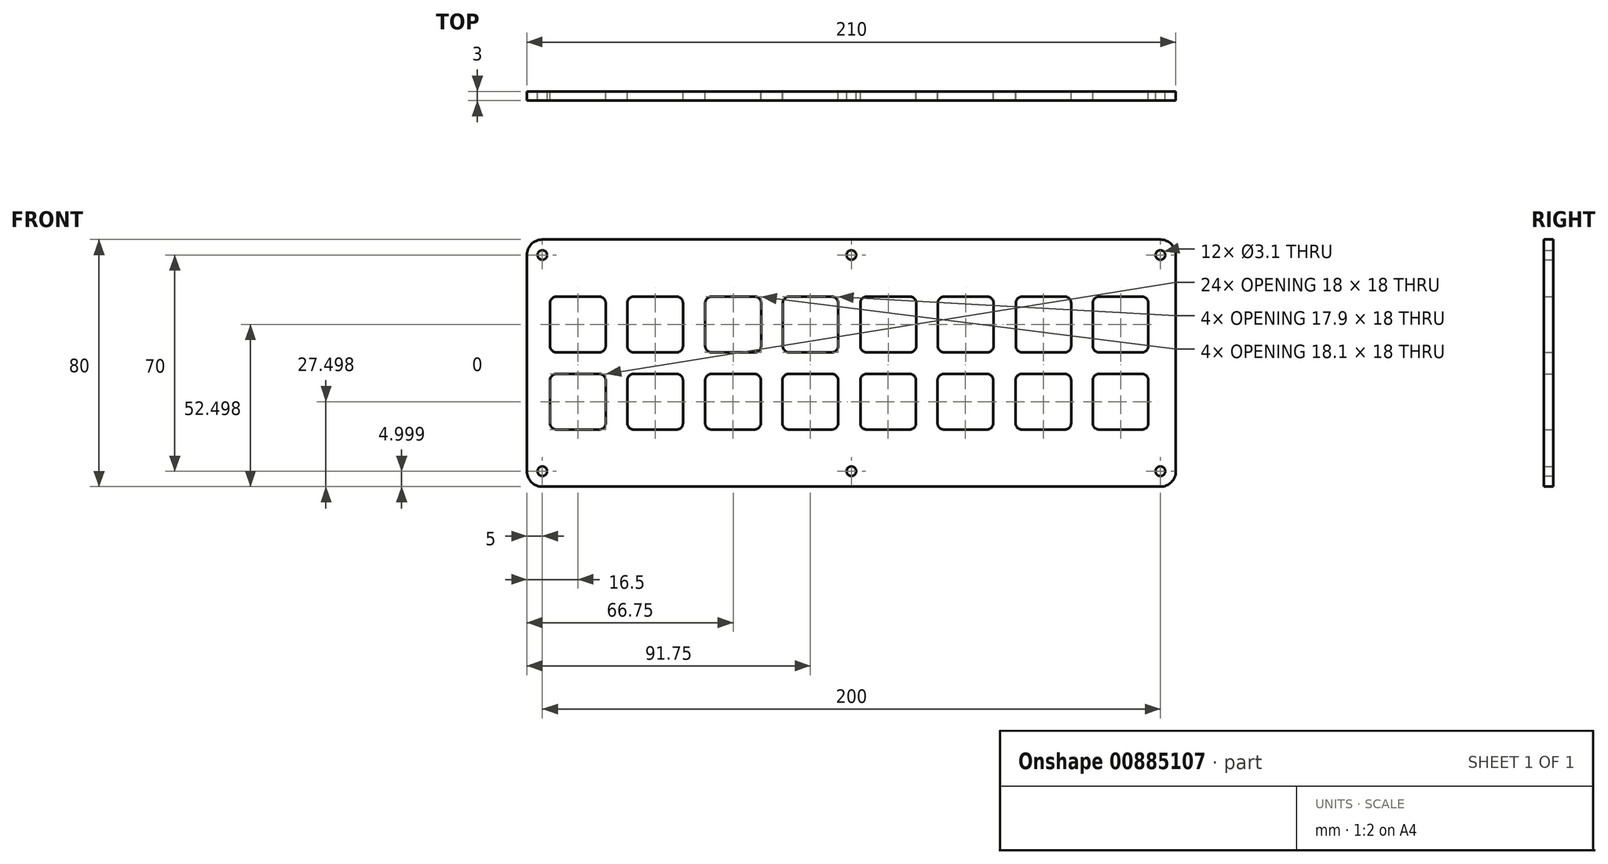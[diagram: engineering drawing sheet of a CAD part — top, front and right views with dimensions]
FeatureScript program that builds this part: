
annotation { "Feature Type Name" : "Feature", "Feature Type Description" : "" }
export const myFeature = defineFeature(function(context is Context, id is Id, definition is map)
    precondition{}
    {
        {
            var Q0;
            Q0=qCreatedBy(makeId("Front.planeOp"),FACE);
            var sketch = newSketch(context, id + "F0", { "sketchPlane" : qUnion([Q0])});
            skLineSegment(sketch, "E0.bottom", {"start": v(-115.46, 43.19) * mm, "end": v(84.54, 43.19) * mm});
            skLineSegment(sketch, "E0.top", {"start": v(-115.46, -36.81) * mm, "end": v(84.54, -36.81) * mm});
            skLineSegment(sketch, "E0.left", {"start": v(-120.46, 38.19) * mm, "end": v(-120.46, -31.81) * mm});
            skLineSegment(sketch, "E0.right", {"start": v(89.54, 38.19) * mm, "end": v(89.54, -31.81) * mm});
            skPoint(sketch, "E1.visualSharp", {"position": v(-120.46, 43.19) * mm});
            skArc(sketch, "E1.filletArc", {"start": v(-115.46, 43.19) * mm, "mid": v(-119, 41.72) * mm, "end": v(-120.46, 38.19) * mm});
            skPoint(sketch, "E2.visualSharp", {"position": v(-120.46, -36.81) * mm});
            skArc(sketch, "E2.filletArc", {"start": v(-120.46, -31.81) * mm, "mid": v(-119, -35.35) * mm, "end": v(-115.46, -36.81) * mm});
            skPoint(sketch, "E3.visualSharp", {"position": v(89.54, 43.19) * mm});
            skArc(sketch, "E3.filletArc", {"start": v(89.54, 38.19) * mm, "mid": v(88.08, 41.72) * mm, "end": v(84.54, 43.19) * mm});
            skPoint(sketch, "E4.visualSharp", {"position": v(89.54, -36.81) * mm});
            skArc(sketch, "E4.filletArc", {"start": v(84.54, -36.81) * mm, "mid": v(88.08, -35.35) * mm, "end": v(89.54, -31.81) * mm});
            skCircle(sketch, "E5", {"center": v(-115.46, 38.19) * mm, "radius": 1.55 * mm});
            skCircle(sketch, "E6", {"center": v(-115.46, -31.81) * mm, "radius": 1.55 * mm});
            skCircle(sketch, "E7", {"center": v(84.54, -31.81) * mm, "radius": 1.55 * mm});
            skCircle(sketch, "E8", {"center": v(84.54, 38.19) * mm, "radius": 1.55 * mm});
            skLineSegment(sketch, "E9.bottom", {"start": v(-110.96, 24.69) * mm, "end": v(-96.96, 24.69) * mm});
            skLineSegment(sketch, "E9.top", {"start": v(-110.96, 6.69) * mm, "end": v(-96.96, 6.69) * mm});
            skLineSegment(sketch, "E9.left", {"start": v(-112.96, 22.69) * mm, "end": v(-112.96, 8.69) * mm});
            skLineSegment(sketch, "E9.right", {"start": v(-94.96, 22.69) * mm, "end": v(-94.96, 8.69) * mm});
            skLineSegment(sketch, "E10.bottom", {"start": v(-71.96, 6.69) * mm, "end": v(-85.96, 6.69) * mm});
            skLineSegment(sketch, "E10.top", {"start": v(-71.96, 24.69) * mm, "end": v(-85.96, 24.69) * mm});
            skLineSegment(sketch, "E10.left", {"start": v(-69.96, 8.69) * mm, "end": v(-69.96, 22.69) * mm});
            skLineSegment(sketch, "E10.right", {"start": v(-87.96, 8.69) * mm, "end": v(-87.96, 22.69) * mm});
            skLineSegment(sketch, "E11.bottom", {"start": v(-110.96, -0.31) * mm, "end": v(-96.96, -0.31) * mm});
            skLineSegment(sketch, "E11.top", {"start": v(-110.96, -18.31) * mm, "end": v(-96.96, -18.31) * mm});
            skLineSegment(sketch, "E11.left", {"start": v(-112.96, -2.31) * mm, "end": v(-112.96, -16.31) * mm});
            skLineSegment(sketch, "E11.right", {"start": v(-94.96, -2.31) * mm, "end": v(-94.96, -16.31) * mm});
            skLineSegment(sketch, "E12.bottom", {"start": v(-85.96, -0.31) * mm, "end": v(-71.96, -0.31) * mm});
            skLineSegment(sketch, "E12.top", {"start": v(-85.96, -18.31) * mm, "end": v(-71.96, -18.31) * mm});
            skLineSegment(sketch, "E12.left", {"start": v(-87.96, -2.31) * mm, "end": v(-87.96, -16.31) * mm});
            skLineSegment(sketch, "E12.right", {"start": v(-69.96, -2.31) * mm, "end": v(-69.96, -16.31) * mm});
            skLineSegment(sketch, "E13.bottom", {"start": v(-60.76, 24.69) * mm, "end": v(-46.66, 24.69) * mm});
            skLineSegment(sketch, "E13.top", {"start": v(-60.76, 6.69) * mm, "end": v(-46.66, 6.69) * mm});
            skLineSegment(sketch, "E13.left", {"start": v(-62.76, 22.69) * mm, "end": v(-62.76, 8.69) * mm});
            skLineSegment(sketch, "E13.right", {"start": v(-44.66, 22.69) * mm, "end": v(-44.66, 8.69) * mm});
            skLineSegment(sketch, "E14.bottom", {"start": v(-35.66, 24.69) * mm, "end": v(-21.76, 24.69) * mm});
            skLineSegment(sketch, "E14.top", {"start": v(-35.66, 6.69) * mm, "end": v(-21.76, 6.69) * mm});
            skLineSegment(sketch, "E14.left", {"start": v(-37.66, 22.69) * mm, "end": v(-37.66, 8.69) * mm});
            skLineSegment(sketch, "E14.right", {"start": v(-19.76, 22.69) * mm, "end": v(-19.76, 8.69) * mm});
            skLineSegment(sketch, "E15.bottom", {"start": v(-60.76, -0.31) * mm, "end": v(-46.76, -0.31) * mm});
            skLineSegment(sketch, "E15.top", {"start": v(-60.76, -18.31) * mm, "end": v(-46.76, -18.31) * mm});
            skLineSegment(sketch, "E15.left", {"start": v(-62.76, -2.31) * mm, "end": v(-62.76, -16.31) * mm});
            skLineSegment(sketch, "E15.right", {"start": v(-44.76, -2.31) * mm, "end": v(-44.76, -16.31) * mm});
            skLineSegment(sketch, "E16.bottom", {"start": v(-35.76, -0.31) * mm, "end": v(-21.76, -0.31) * mm});
            skLineSegment(sketch, "E16.top", {"start": v(-35.76, -18.31) * mm, "end": v(-21.76, -18.31) * mm});
            skLineSegment(sketch, "E16.left", {"start": v(-37.76, -2.31) * mm, "end": v(-37.76, -16.31) * mm});
            skLineSegment(sketch, "E16.right", {"start": v(-19.76, -2.31) * mm, "end": v(-19.76, -16.31) * mm});
            skLineSegment(sketch, "E17.bottom", {"start": v(-10.56, 24.69) * mm, "end": v(3.54, 24.69) * mm});
            skLineSegment(sketch, "E17.top", {"start": v(-10.56, 6.69) * mm, "end": v(3.54, 6.69) * mm});
            skLineSegment(sketch, "E17.left", {"start": v(-12.56, 22.69) * mm, "end": v(-12.56, 8.69) * mm});
            skLineSegment(sketch, "E17.right", {"start": v(5.54, 22.69) * mm, "end": v(5.54, 8.69) * mm});
            skLineSegment(sketch, "E18.bottom", {"start": v(-10.56, -0.31) * mm, "end": v(3.44, -0.31) * mm});
            skLineSegment(sketch, "E18.top", {"start": v(-10.56, -18.31) * mm, "end": v(3.44, -18.31) * mm});
            skLineSegment(sketch, "E18.left", {"start": v(-12.56, -2.31) * mm, "end": v(-12.56, -16.31) * mm});
            skLineSegment(sketch, "E18.right", {"start": v(5.44, -2.31) * mm, "end": v(5.44, -16.31) * mm});
            skLineSegment(sketch, "E19.bottom", {"start": v(14.54, 24.69) * mm, "end": v(28.54, 24.69) * mm});
            skLineSegment(sketch, "E19.top", {"start": v(14.54, 6.69) * mm, "end": v(28.54, 6.69) * mm});
            skLineSegment(sketch, "E19.left", {"start": v(12.54, 22.69) * mm, "end": v(12.54, 8.69) * mm});
            skLineSegment(sketch, "E19.right", {"start": v(30.54, 22.69) * mm, "end": v(30.54, 8.69) * mm});
            skLineSegment(sketch, "E20.bottom", {"start": v(14.44, -0.31) * mm, "end": v(28.44, -0.31) * mm});
            skLineSegment(sketch, "E20.top", {"start": v(14.44, -18.31) * mm, "end": v(28.44, -18.31) * mm});
            skLineSegment(sketch, "E20.left", {"start": v(12.44, -2.31) * mm, "end": v(12.44, -16.31) * mm});
            skLineSegment(sketch, "E20.right", {"start": v(30.44, -2.31) * mm, "end": v(30.44, -16.31) * mm});
            skLineSegment(sketch, "E21.bottom", {"start": v(39.74, 24.69) * mm, "end": v(53.64, 24.69) * mm});
            skLineSegment(sketch, "E21.top", {"start": v(39.74, 6.69) * mm, "end": v(53.64, 6.69) * mm});
            skLineSegment(sketch, "E21.left", {"start": v(37.74, 22.69) * mm, "end": v(37.74, 8.69) * mm});
            skLineSegment(sketch, "E21.right", {"start": v(55.64, 22.69) * mm, "end": v(55.64, 8.69) * mm});
            skLineSegment(sketch, "E22.bottom", {"start": v(64.64, 24.69) * mm, "end": v(78.64, 24.69) * mm});
            skLineSegment(sketch, "E22.top", {"start": v(64.64, 6.69) * mm, "end": v(78.64, 6.69) * mm});
            skLineSegment(sketch, "E22.left", {"start": v(62.64, 22.69) * mm, "end": v(62.64, 8.69) * mm});
            skLineSegment(sketch, "E22.right", {"start": v(80.64, 22.69) * mm, "end": v(80.64, 8.69) * mm});
            skLineSegment(sketch, "E23.bottom", {"start": v(39.64, -0.31) * mm, "end": v(53.64, -0.31) * mm});
            skLineSegment(sketch, "E23.top", {"start": v(39.64, -18.31) * mm, "end": v(53.64, -18.31) * mm});
            skLineSegment(sketch, "E23.left", {"start": v(37.64, -2.31) * mm, "end": v(37.64, -16.31) * mm});
            skLineSegment(sketch, "E23.right", {"start": v(55.64, -2.31) * mm, "end": v(55.64, -16.31) * mm});
            skLineSegment(sketch, "E24.bottom", {"start": v(64.64, -0.31) * mm, "end": v(78.64, -0.31) * mm});
            skLineSegment(sketch, "E24.top", {"start": v(64.64, -18.31) * mm, "end": v(78.64, -18.31) * mm});
            skLineSegment(sketch, "E24.left", {"start": v(62.64, -2.31) * mm, "end": v(62.64, -16.31) * mm});
            skLineSegment(sketch, "E24.right", {"start": v(80.64, -2.31) * mm, "end": v(80.64, -16.31) * mm});
            skPoint(sketch, "E25", {"position": v(-15.46, 38.19) * mm});
            skCircle(sketch, "E26", {"center": v(-15.46, 38.19) * mm, "radius": 1.55 * mm});
            skPoint(sketch, "E27.visualSharp", {"position": v(-112.96, 24.69) * mm});
            skArc(sketch, "E27.filletArc", {"start": v(-110.96, 24.69) * mm, "mid": v(-112.37, 24.1) * mm, "end": v(-112.96, 22.69) * mm});
            skPoint(sketch, "E28.visualSharp", {"position": v(-94.96, 24.69) * mm});
            skArc(sketch, "E28.filletArc", {"start": v(-94.96, 22.69) * mm, "mid": v(-95.55, 24.1) * mm, "end": v(-96.96, 24.69) * mm});
            skPoint(sketch, "E29.visualSharp", {"position": v(-94.96, 6.69) * mm});
            skArc(sketch, "E29.filletArc", {"start": v(-96.96, 6.69) * mm, "mid": v(-95.55, 7.27) * mm, "end": v(-94.96, 8.69) * mm});
            skPoint(sketch, "E30.visualSharp", {"position": v(-112.96, 6.69) * mm});
            skArc(sketch, "E30.filletArc", {"start": v(-112.96, 8.69) * mm, "mid": v(-112.37, 7.27) * mm, "end": v(-110.96, 6.69) * mm});
            skPoint(sketch, "E31.visualSharp", {"position": v(-112.96, -0.31) * mm});
            skArc(sketch, "E31.filletArc", {"start": v(-110.96, -0.31) * mm, "mid": v(-112.37, -0.9) * mm, "end": v(-112.96, -2.31) * mm});
            skPoint(sketch, "E32.visualSharp", {"position": v(-94.96, -0.31) * mm});
            skArc(sketch, "E32.filletArc", {"start": v(-94.96, -2.31) * mm, "mid": v(-95.55, -0.9) * mm, "end": v(-96.96, -0.31) * mm});
            skPoint(sketch, "E33.visualSharp", {"position": v(-94.96, -18.31) * mm});
            skArc(sketch, "E33.filletArc", {"start": v(-96.96, -18.31) * mm, "mid": v(-95.55, -17.73) * mm, "end": v(-94.96, -16.31) * mm});
            skPoint(sketch, "E34.visualSharp", {"position": v(-112.96, -18.31) * mm});
            skArc(sketch, "E34.filletArc", {"start": v(-112.96, -16.31) * mm, "mid": v(-112.37, -17.73) * mm, "end": v(-110.96, -18.31) * mm});
            skPoint(sketch, "E35.visualSharp", {"position": v(-87.96, -0.31) * mm});
            skArc(sketch, "E35.filletArc", {"start": v(-85.96, -0.31) * mm, "mid": v(-87.37, -0.9) * mm, "end": v(-87.96, -2.31) * mm});
            skPoint(sketch, "E36.visualSharp", {"position": v(-69.96, -0.31) * mm});
            skArc(sketch, "E36.filletArc", {"start": v(-69.96, -2.31) * mm, "mid": v(-70.55, -0.9) * mm, "end": v(-71.96, -0.31) * mm});
            skPoint(sketch, "E37.visualSharp", {"position": v(-69.96, -18.31) * mm});
            skArc(sketch, "E37.filletArc", {"start": v(-71.96, -18.31) * mm, "mid": v(-70.55, -17.73) * mm, "end": v(-69.96, -16.31) * mm});
            skPoint(sketch, "E38.visualSharp", {"position": v(-87.96, -18.31) * mm});
            skArc(sketch, "E38.filletArc", {"start": v(-87.96, -16.31) * mm, "mid": v(-87.37, -17.73) * mm, "end": v(-85.96, -18.31) * mm});
            skPoint(sketch, "E39.visualSharp", {"position": v(-87.96, 24.69) * mm});
            skArc(sketch, "E39.filletArc", {"start": v(-85.96, 24.69) * mm, "mid": v(-87.37, 24.1) * mm, "end": v(-87.96, 22.69) * mm});
            skPoint(sketch, "E40.visualSharp", {"position": v(-69.96, 24.69) * mm});
            skArc(sketch, "E40.filletArc", {"start": v(-69.96, 22.69) * mm, "mid": v(-70.55, 24.1) * mm, "end": v(-71.96, 24.69) * mm});
            skPoint(sketch, "E41.visualSharp", {"position": v(-69.96, 6.69) * mm});
            skArc(sketch, "E41.filletArc", {"start": v(-71.96, 6.69) * mm, "mid": v(-70.55, 7.27) * mm, "end": v(-69.96, 8.69) * mm});
            skPoint(sketch, "E42.visualSharp", {"position": v(-87.96, 6.69) * mm});
            skArc(sketch, "E42.filletArc", {"start": v(-87.96, 8.69) * mm, "mid": v(-87.37, 7.27) * mm, "end": v(-85.96, 6.69) * mm});
            skPoint(sketch, "E43.visualSharp", {"position": v(-62.76, 24.69) * mm});
            skArc(sketch, "E43.filletArc", {"start": v(-60.76, 24.69) * mm, "mid": v(-62.17, 24.1) * mm, "end": v(-62.76, 22.69) * mm});
            skPoint(sketch, "E44.visualSharp", {"position": v(-44.66, 24.69) * mm});
            skArc(sketch, "E44.filletArc", {"start": v(-44.66, 22.69) * mm, "mid": v(-45.25, 24.1) * mm, "end": v(-46.66, 24.69) * mm});
            skPoint(sketch, "E45.visualSharp", {"position": v(-44.66, 6.69) * mm});
            skArc(sketch, "E45.filletArc", {"start": v(-46.66, 6.69) * mm, "mid": v(-45.25, 7.27) * mm, "end": v(-44.66, 8.69) * mm});
            skPoint(sketch, "E46.visualSharp", {"position": v(-62.76, 6.69) * mm});
            skArc(sketch, "E46.filletArc", {"start": v(-62.76, 8.69) * mm, "mid": v(-62.17, 7.27) * mm, "end": v(-60.76, 6.69) * mm});
            skPoint(sketch, "E47.visualSharp", {"position": v(-62.76, -0.31) * mm});
            skArc(sketch, "E47.filletArc", {"start": v(-60.76, -0.31) * mm, "mid": v(-62.17, -0.9) * mm, "end": v(-62.76, -2.31) * mm});
            skPoint(sketch, "E48.visualSharp", {"position": v(-44.76, -0.31) * mm});
            skArc(sketch, "E48.filletArc", {"start": v(-44.76, -2.31) * mm, "mid": v(-45.35, -0.9) * mm, "end": v(-46.76, -0.31) * mm});
            skPoint(sketch, "E49.visualSharp", {"position": v(-44.76, -18.31) * mm});
            skArc(sketch, "E49.filletArc", {"start": v(-46.76, -18.31) * mm, "mid": v(-45.35, -17.73) * mm, "end": v(-44.76, -16.31) * mm});
            skPoint(sketch, "E50.visualSharp", {"position": v(-62.76, -18.31) * mm});
            skArc(sketch, "E50.filletArc", {"start": v(-62.76, -16.31) * mm, "mid": v(-62.17, -17.73) * mm, "end": v(-60.76, -18.31) * mm});
            skPoint(sketch, "E51.visualSharp", {"position": v(-37.76, -18.31) * mm});
            skArc(sketch, "E51.filletArc", {"start": v(-37.76, -16.31) * mm, "mid": v(-37.17, -17.73) * mm, "end": v(-35.76, -18.31) * mm});
            skPoint(sketch, "E52.visualSharp", {"position": v(-37.76, -0.31) * mm});
            skArc(sketch, "E52.filletArc", {"start": v(-35.76, -0.31) * mm, "mid": v(-37.17, -0.9) * mm, "end": v(-37.76, -2.31) * mm});
            skPoint(sketch, "E53.visualSharp", {"position": v(-19.76, -0.31) * mm});
            skArc(sketch, "E53.filletArc", {"start": v(-19.76, -2.31) * mm, "mid": v(-20.35, -0.9) * mm, "end": v(-21.76, -0.31) * mm});
            skPoint(sketch, "E54.visualSharp", {"position": v(-19.76, -18.31) * mm});
            skArc(sketch, "E54.filletArc", {"start": v(-21.76, -18.31) * mm, "mid": v(-20.35, -17.73) * mm, "end": v(-19.76, -16.31) * mm});
            skPoint(sketch, "E55.visualSharp", {"position": v(-37.66, 6.69) * mm});
            skArc(sketch, "E55.filletArc", {"start": v(-37.66, 8.69) * mm, "mid": v(-37.07, 7.27) * mm, "end": v(-35.66, 6.69) * mm});
            skPoint(sketch, "E56.visualSharp", {"position": v(-37.66, 24.69) * mm});
            skArc(sketch, "E56.filletArc", {"start": v(-35.66, 24.69) * mm, "mid": v(-37.07, 24.1) * mm, "end": v(-37.66, 22.69) * mm});
            skPoint(sketch, "E57.visualSharp", {"position": v(-19.76, 24.69) * mm});
            skArc(sketch, "E57.filletArc", {"start": v(-19.76, 22.69) * mm, "mid": v(-20.35, 24.1) * mm, "end": v(-21.76, 24.69) * mm});
            skPoint(sketch, "E58.visualSharp", {"position": v(-19.76, 6.69) * mm});
            skArc(sketch, "E58.filletArc", {"start": v(-21.76, 6.69) * mm, "mid": v(-20.35, 7.27) * mm, "end": v(-19.76, 8.69) * mm});
            skPoint(sketch, "E59.visualSharp", {"position": v(-12.56, 24.69) * mm});
            skArc(sketch, "E59.filletArc", {"start": v(-10.56, 24.69) * mm, "mid": v(-11.97, 24.1) * mm, "end": v(-12.56, 22.69) * mm});
            skPoint(sketch, "E60.visualSharp", {"position": v(5.54, 24.69) * mm});
            skArc(sketch, "E60.filletArc", {"start": v(5.54, 22.69) * mm, "mid": v(4.95, 24.1) * mm, "end": v(3.54, 24.69) * mm});
            skPoint(sketch, "E61.visualSharp", {"position": v(5.54, 6.69) * mm});
            skArc(sketch, "E61.filletArc", {"start": v(3.54, 6.69) * mm, "mid": v(4.95, 7.27) * mm, "end": v(5.54, 8.69) * mm});
            skPoint(sketch, "E62.visualSharp", {"position": v(-12.56, 6.69) * mm});
            skArc(sketch, "E62.filletArc", {"start": v(-12.56, 8.69) * mm, "mid": v(-11.97, 7.27) * mm, "end": v(-10.56, 6.69) * mm});
            skPoint(sketch, "E63.visualSharp", {"position": v(-12.56, -0.31) * mm});
            skArc(sketch, "E63.filletArc", {"start": v(-10.56, -0.31) * mm, "mid": v(-11.97, -0.9) * mm, "end": v(-12.56, -2.31) * mm});
            skPoint(sketch, "E64.visualSharp", {"position": v(5.44, -0.31) * mm});
            skArc(sketch, "E64.filletArc", {"start": v(5.44, -2.31) * mm, "mid": v(4.85, -0.9) * mm, "end": v(3.44, -0.31) * mm});
            skPoint(sketch, "E65.visualSharp", {"position": v(5.44, -18.31) * mm});
            skArc(sketch, "E65.filletArc", {"start": v(3.44, -18.31) * mm, "mid": v(4.85, -17.73) * mm, "end": v(5.44, -16.31) * mm});
            skPoint(sketch, "E66.visualSharp", {"position": v(-12.56, -18.31) * mm});
            skArc(sketch, "E66.filletArc", {"start": v(-12.56, -16.31) * mm, "mid": v(-11.97, -17.73) * mm, "end": v(-10.56, -18.31) * mm});
            skPoint(sketch, "E67.visualSharp", {"position": v(12.44, -0.31) * mm});
            skArc(sketch, "E67.filletArc", {"start": v(14.44, -0.31) * mm, "mid": v(13.03, -0.9) * mm, "end": v(12.44, -2.31) * mm});
            skPoint(sketch, "E68.visualSharp", {"position": v(30.44, -0.31) * mm});
            skArc(sketch, "E68.filletArc", {"start": v(30.44, -2.31) * mm, "mid": v(29.85, -0.9) * mm, "end": v(28.44, -0.31) * mm});
            skPoint(sketch, "E69.visualSharp", {"position": v(30.44, -18.31) * mm});
            skArc(sketch, "E69.filletArc", {"start": v(28.44, -18.31) * mm, "mid": v(29.85, -17.73) * mm, "end": v(30.44, -16.31) * mm});
            skPoint(sketch, "E70.visualSharp", {"position": v(12.44, -18.31) * mm});
            skArc(sketch, "E70.filletArc", {"start": v(12.44, -16.31) * mm, "mid": v(13.03, -17.73) * mm, "end": v(14.44, -18.31) * mm});
            skPoint(sketch, "E71.visualSharp", {"position": v(30.54, 24.69) * mm});
            skArc(sketch, "E71.filletArc", {"start": v(30.54, 22.69) * mm, "mid": v(29.95, 24.1) * mm, "end": v(28.54, 24.69) * mm});
            skPoint(sketch, "E72.visualSharp", {"position": v(12.54, 24.69) * mm});
            skArc(sketch, "E72.filletArc", {"start": v(14.54, 24.69) * mm, "mid": v(13.13, 24.1) * mm, "end": v(12.54, 22.69) * mm});
            skPoint(sketch, "E73.visualSharp", {"position": v(12.54, 6.69) * mm});
            skArc(sketch, "E73.filletArc", {"start": v(12.54, 8.69) * mm, "mid": v(13.13, 7.27) * mm, "end": v(14.54, 6.69) * mm});
            skPoint(sketch, "E74.visualSharp", {"position": v(30.54, 6.69) * mm});
            skArc(sketch, "E74.filletArc", {"start": v(28.54, 6.69) * mm, "mid": v(29.95, 7.27) * mm, "end": v(30.54, 8.69) * mm});
            skPoint(sketch, "E75.visualSharp", {"position": v(37.74, 24.69) * mm});
            skArc(sketch, "E75.filletArc", {"start": v(39.74, 24.69) * mm, "mid": v(38.33, 24.1) * mm, "end": v(37.74, 22.69) * mm});
            skPoint(sketch, "E76.visualSharp", {"position": v(55.64, 24.69) * mm});
            skArc(sketch, "E76.filletArc", {"start": v(55.64, 22.69) * mm, "mid": v(55.05, 24.1) * mm, "end": v(53.64, 24.69) * mm});
            skPoint(sketch, "E77.visualSharp", {"position": v(55.64, 6.69) * mm});
            skArc(sketch, "E77.filletArc", {"start": v(53.64, 6.69) * mm, "mid": v(55.05, 7.27) * mm, "end": v(55.64, 8.69) * mm});
            skPoint(sketch, "E78.visualSharp", {"position": v(37.74, 6.69) * mm});
            skArc(sketch, "E78.filletArc", {"start": v(37.74, 8.69) * mm, "mid": v(38.33, 7.27) * mm, "end": v(39.74, 6.69) * mm});
            skPoint(sketch, "E79.visualSharp", {"position": v(37.64, -0.31) * mm});
            skArc(sketch, "E79.filletArc", {"start": v(39.64, -0.31) * mm, "mid": v(38.23, -0.9) * mm, "end": v(37.64, -2.31) * mm});
            skPoint(sketch, "E80.visualSharp", {"position": v(55.64, -0.31) * mm});
            skArc(sketch, "E80.filletArc", {"start": v(55.64, -2.31) * mm, "mid": v(55.05, -0.9) * mm, "end": v(53.64, -0.31) * mm});
            skPoint(sketch, "E81.visualSharp", {"position": v(55.64, -18.31) * mm});
            skArc(sketch, "E81.filletArc", {"start": v(53.64, -18.31) * mm, "mid": v(55.05, -17.73) * mm, "end": v(55.64, -16.31) * mm});
            skPoint(sketch, "E82.visualSharp", {"position": v(37.64, -18.31) * mm});
            skArc(sketch, "E82.filletArc", {"start": v(37.64, -16.31) * mm, "mid": v(38.23, -17.73) * mm, "end": v(39.64, -18.31) * mm});
            skPoint(sketch, "E83.visualSharp", {"position": v(62.64, -18.31) * mm});
            skArc(sketch, "E83.filletArc", {"start": v(62.64, -16.31) * mm, "mid": v(63.23, -17.73) * mm, "end": v(64.64, -18.31) * mm});
            skPoint(sketch, "E84.visualSharp", {"position": v(62.64, -0.31) * mm});
            skArc(sketch, "E84.filletArc", {"start": v(64.64, -0.31) * mm, "mid": v(63.23, -0.9) * mm, "end": v(62.64, -2.31) * mm});
            skPoint(sketch, "E85.visualSharp", {"position": v(80.64, -0.31) * mm});
            skArc(sketch, "E85.filletArc", {"start": v(80.64, -2.31) * mm, "mid": v(80.05, -0.9) * mm, "end": v(78.64, -0.31) * mm});
            skPoint(sketch, "E86.visualSharp", {"position": v(80.64, -18.31) * mm});
            skArc(sketch, "E86.filletArc", {"start": v(78.64, -18.31) * mm, "mid": v(80.05, -17.73) * mm, "end": v(80.64, -16.31) * mm});
            skPoint(sketch, "E87.visualSharp", {"position": v(62.64, 6.69) * mm});
            skArc(sketch, "E87.filletArc", {"start": v(62.64, 8.69) * mm, "mid": v(63.23, 7.27) * mm, "end": v(64.64, 6.69) * mm});
            skPoint(sketch, "E88.visualSharp", {"position": v(62.64, 24.69) * mm});
            skArc(sketch, "E88.filletArc", {"start": v(64.64, 24.69) * mm, "mid": v(63.23, 24.1) * mm, "end": v(62.64, 22.69) * mm});
            skPoint(sketch, "E89.visualSharp", {"position": v(80.64, 24.69) * mm});
            skArc(sketch, "E89.filletArc", {"start": v(80.64, 22.69) * mm, "mid": v(80.05, 24.1) * mm, "end": v(78.64, 24.69) * mm});
            skPoint(sketch, "E90.visualSharp", {"position": v(80.64, 6.69) * mm});
            skArc(sketch, "E90.filletArc", {"start": v(78.64, 6.69) * mm, "mid": v(80.05, 7.27) * mm, "end": v(80.64, 8.69) * mm});
            skCircle(sketch, "E91", {"center": v(-15.46, -31.81) * mm, "radius": 1.55 * mm});
            skLineSegment(sketch, "E92", {"start": v(33.48, 56.27) * mm, "end": v(33.48, 66.27) * mm});
            skLineSegment(sketch, "E93", {"start": v(33.48, 66.27) * mm, "end": v(45.48, 66.27) * mm});
            skLineSegment(sketch, "E94", {"start": v(45.48, 66.27) * mm, "end": v(45.48, 56.27) * mm});
            skLineSegment(sketch, "E95", {"start": v(45.48, 56.27) * mm, "end": v(41.48, 56.27) * mm});
            skLineSegment(sketch, "E96", {"start": v(41.48, 56.27) * mm, "end": v(41.48, 61.27) * mm});
            skLineSegment(sketch, "E97", {"start": v(41.48, 61.27) * mm, "end": v(43.98, 61.27) * mm});
            skLineSegment(sketch, "E98", {"start": v(43.98, 61.27) * mm, "end": v(43.98, 65.27) * mm});
            skLineSegment(sketch, "E99", {"start": v(33.48, 56.27) * mm, "end": v(37.48, 56.27) * mm});
            skLineSegment(sketch, "E100", {"start": v(37.48, 56.27) * mm, "end": v(37.48, 61.27) * mm});
            skLineSegment(sketch, "E101", {"start": v(37.48, 61.27) * mm, "end": v(34.98, 61.27) * mm});
            skLineSegment(sketch, "E102", {"start": v(34.98, 61.27) * mm, "end": v(34.98, 65.27) * mm});
            skLineSegment(sketch, "E103", {"start": v(34.98, 65.27) * mm, "end": v(43.98, 65.27) * mm});
            skSolve(sketch);
        }
        {
            var Q0;
            Q0=makeQuery(id+"F0.imprint","IMPRINT",FACE,{"disambiguationData":[TD([[makeQuery(id+"F0.imprint","IMPRINT",EDGE,{"derivedFrom":sQuery(id+"F0.wireOp",EDGE,"E0.bottom")}),-1.0]])]});
            extrude(context, id + "F1", {"entities" : qUnion([Q0]), "depth" : 3 * mm, "offsetDistance" : 25 * mm});
        }
    });
